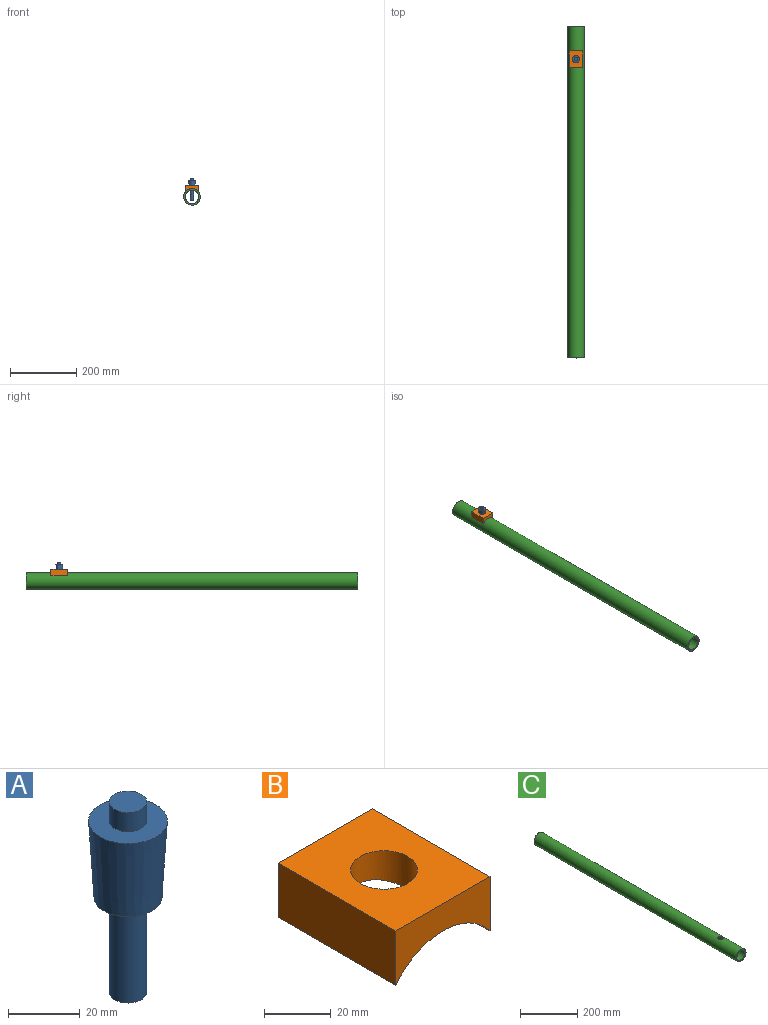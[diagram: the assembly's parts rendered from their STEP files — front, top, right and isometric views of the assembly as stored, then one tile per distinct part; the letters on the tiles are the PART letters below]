
ASSEMBLY  parts=3 mates=1
PART A: 7 faces, bbox 22x22x65 mm
  f0: plane 22x22mm, normal (0,0,1), area 293.5mm2, adj f2,f5
  f1: plane 19x19mm, normal (0,0,-1), area 196.9mm2, adj f2,f4
  f2: cone r=11mm half-angle=3.3deg, axis (0,0,1), area 1677.3mm2, adj f0,f1
  f3: plane 10.5x10.5mm, normal (0,0,-1), area 86.6mm2, adj f4
  f4: cylinder r=5.25mm len=32.5mm, axis (0,0,-1), area 1072.1mm2, adj f1,f3
  f5: cylinder r=5.25mm len=10.5mm, axis (0,0,-1), area 214.4mm2, adj f0,f6
  f6: plane 10.5x10.5mm, normal (0,0,1), area 86.6mm2, adj f5
PART B: 7 faces, bbox 40x50x19.9 mm
  f0: cylinder r=25mm len=50mm, axis (0,1,0), area 1997.1mm2, adj f1,f2,f3,f5,f6
  f1: plane 50x19.91mm, normal (-1,0,0), area 995.6mm2, adj f0,f3,f4,f5
  f2: plane 50x19.91mm, normal (1,0,0), area 995.6mm2, adj f0,f3,f4,f5
  f3: plane 40x19.91mm, normal (0,1,0), area 516.9mm2, adj f0,f1,f2,f4
  f4: plane 50x40mm, normal (0,0,1), area 1685.8mm2, adj f1,f2,f3,f5,f6
  f5: plane 40x19.91mm, normal (0,-1,0), area 516.9mm2, adj f0,f1,f2,f4
  f6: cylinder r=10mm len=20mm, axis (0,0,-1), area 687.5mm2, adj f0,f4
PART C: 5 faces, bbox 50x1000x50 mm
  f0: cylinder r=25mm len=1000mm, axis (0,-1,0), area 156758.8mm2, adj f2,f3,f4
  f1: cylinder r=20mm len=1000mm, axis (0,-1,0), area 125337.9mm2, adj f2,f3,f4
  f2: plane 50x50mm, normal (0,1,0), area 706.9mm2, adj f0,f1
  f3: plane 50x50mm, normal (0,-1,0), area 706.9mm2, adj f0,f1
  f4: cylinder r=10mm len=20mm, axis (0,0,-1), area 331.9mm2, adj f0,f1
PLACE A t=(0,0,0.76)mm
PLACE B t=(0,25,-6.15)mm
PLACE C rot(axis=(0,0,1),180deg) t=(0,100,-21.15)mm
MATE ball A.f2 <-> B.f6  axis (0,0,1) through (0,0,13.76)mm
